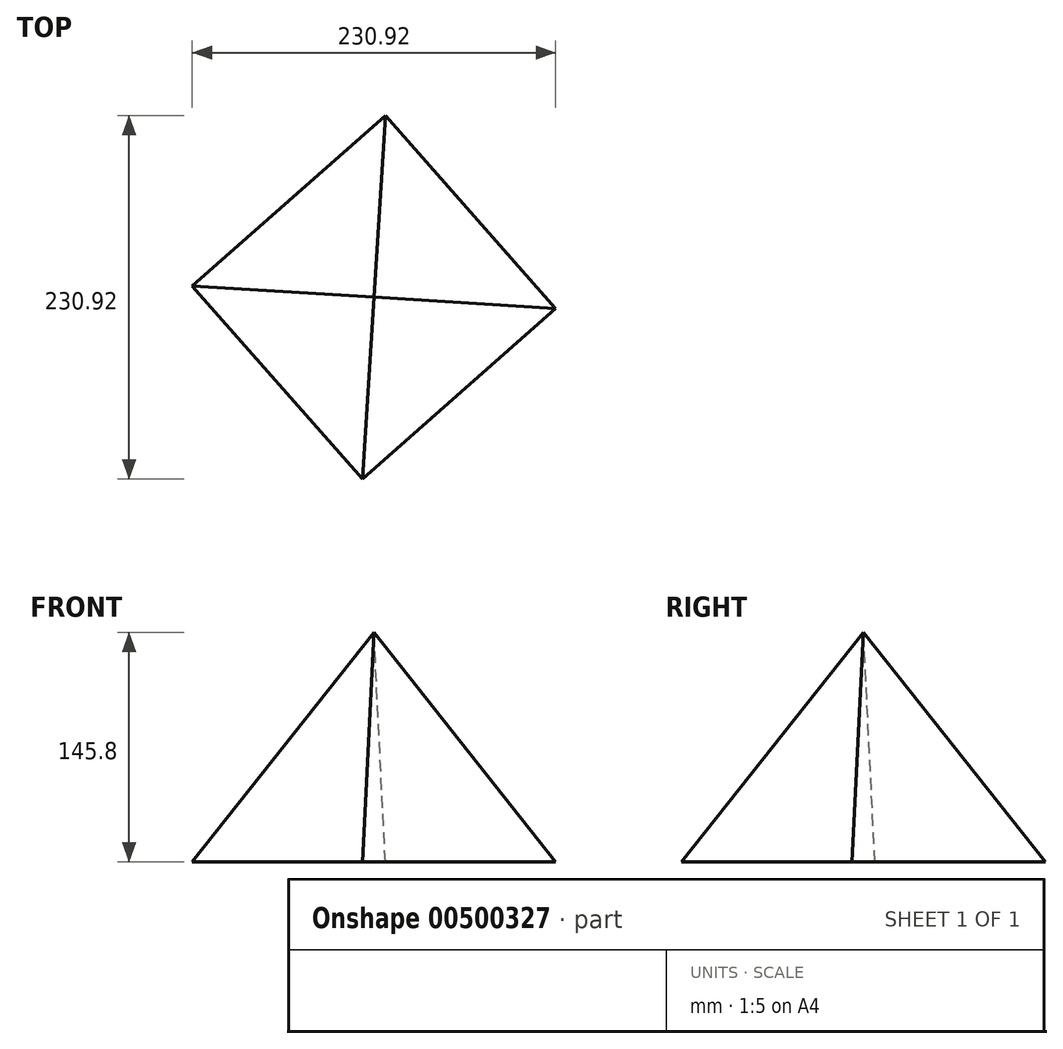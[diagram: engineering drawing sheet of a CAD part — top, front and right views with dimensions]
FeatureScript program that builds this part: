
annotation { "Feature Type Name" : "Feature", "Feature Type Description" : "" }
export const myFeature = defineFeature(function(context is Context, id is Id, definition is map)
    precondition{}
    {
        {
            var Q0;
            Q0=qCreatedBy(makeId("Top.planeOp"),FACE);
            var sketch = newSketch(context, id + "F0", { "sketchPlane" : qUnion([Q0])});
            skCircle(sketch, "E0.cCircle", {"center": v(0, 0) * mm, "radius": 115.69 * mm, "construction": true});
            skLineSegment(sketch, "E0.0", {"start": v(7.25, 115.46) * mm, "end": v(115.46, -7.25) * mm});
            skLineSegment(sketch, "E0.1", {"start": v(115.46, -7.25) * mm, "end": v(-7.25, -115.46) * mm});
            skLineSegment(sketch, "E0.2", {"start": v(-7.25, -115.46) * mm, "end": v(-115.46, 7.25) * mm});
            skLineSegment(sketch, "E0.3", {"start": v(-115.46, 7.25) * mm, "end": v(7.25, 115.46) * mm});
            skSolve(sketch);
        }
        {
            var Q0;
            Q0=qCreatedBy(makeId("Top.planeOp"),FACE);
            cPlane(context, id + "F1", {"entities" : qUnion([Q0]), "cplaneType" : CPlaneType.OFFSET, "offset" : 145.8 * mm, "width" : 152.4 * mm, "height" : 152.4 * mm});
        }
        {
            var Q0;
            Q0=qCreatedBy(id+"F1.planeOp",FACE);
            var sketch = newSketch(context, id + "F2", { "sketchPlane" : qUnion([Q0])});
            skPoint(sketch, "E1", {"position": v(0, 0) * mm});
            skSolve(sketch);
        }
        {
            var Q0;
            Q0=makeQuery(id+"F0.imprint","IMPRINT",FACE,{"disambiguationData":[TD([[makeQuery(id+"F0.imprint","IMPRINT",EDGE,{"derivedFrom":sQuery(id+"F0.wireOp",EDGE,"E0.0")}),-1.0]])]});
            var Q1;
            Q1=sQuery(id+"F2.wireOp",VERTEX,"E1");
            loft(context, id + "F3", {"sheetProfilesArray" : [{ "sheetProfileEntities" : qUnion([Q0]) }, { "sheetProfileEntities" : qUnion([Q1]) }]});
        }
    });
